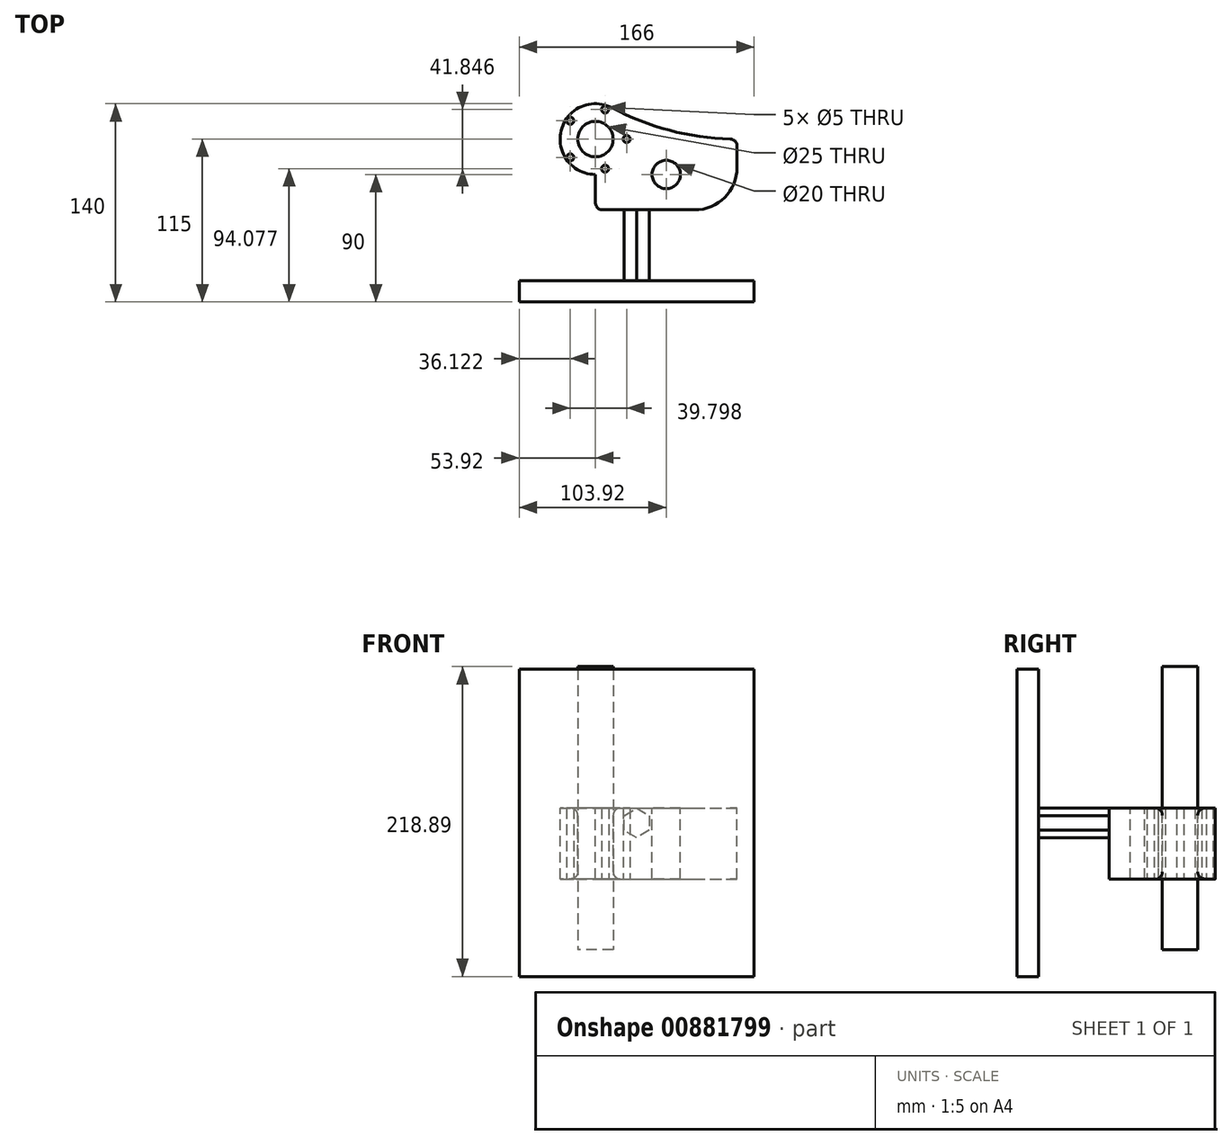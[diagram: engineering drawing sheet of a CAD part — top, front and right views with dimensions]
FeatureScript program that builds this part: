
annotation { "Feature Type Name" : "Feature", "Feature Type Description" : "" }
export const myFeature = defineFeature(function(context is Context, id is Id, definition is map)
    precondition{}
    {
        {
            var Q0;
            Q0=qCreatedBy(makeId("Top.planeOp"),FACE);
            var sketch = newSketch(context, id + "F0", { "sketchPlane" : qUnion([Q0])});
            skLineSegment(sketch, "E0.bottom", {"start": v(-50, -25) * mm, "end": v(50, -25) * mm});
            skLineSegment(sketch, "E0.top", {"start": v(-50, 25) * mm, "end": v(50, 25) * mm});
            skLineSegment(sketch, "E0.left", {"start": v(-50, -25) * mm, "end": v(-50, 25) * mm});
            skLineSegment(sketch, "E0.right", {"start": v(50, -25) * mm, "end": v(50, 25) * mm});
            skPoint(sketch, "E0.middle", {"position": v(0, 0) * mm});
            skCircle(sketch, "E1", {"center": v(-50, 25) * mm, "radius": 25 * mm});
            skArc(sketch, "E2", {"start": v(-38.24, 47.06) * mm, "mid": v(4.52, 30.6) * mm, "end": v(50, 25) * mm});
            skCircle(sketch, "E3", {"center": v(-50, 25) * mm, "radius": 12.5 * mm});
            skSolve(sketch);
        }
        {
            var Q0;
            {var subQ0=sQuery(id+"F0.wireOp",EDGE,"E2");Q0=makeQuery(id+"F0.imprint","IMPRINT",FACE,{"disambiguationData":[TD([[makeQuery(id+"F0.imprint","IMPRINT",EDGE,{"derivedFrom":subQ0}),-1.0]])]});}
            var Q1;
            {var subQ1=sQuery(id+"F0.wireOp",EDGE,"E0.bottom");Q1=makeQuery(id+"F0.imprint","IMPRINT",FACE,{"disambiguationData":[TD([[makeQuery(id+"F0.imprint","IMPRINT",EDGE,{"derivedFrom":subQ1}),1.0]])]});}
            var Q2;
            {var subQ4=sQuery(id+"F0.wireOp",EDGE,"E0.top");var subQ6=sQuery(id+"F0.wireOp",EDGE,"E3");var subQ8=makeQuery(id+"F0.imprint","INTERSECT",VERTEX,{"derivedFrom":[subQ4,subQ6]});Q2=makeQuery(id+"F0.imprint","IMPRINT",FACE,{"disambiguationData":[TD([[makeQuery(id+"F0.imprint","IMPRINT",EDGE,{"disambiguationData":[TD([[subQ8,-1.0]])],"derivedFrom":subQ4}),1.0]])]});}
            var Q3;
            {var subQ0=sQuery(id+"F0.wireOp",EDGE,"E3");var subQ1=sQuery(id+"F0.wireOp",EDGE,"E0.top");var subQ2=makeQuery(id+"F0.imprint","INTERSECT",VERTEX,{"derivedFrom":[subQ1,subQ0]});Q3=makeQuery(id+"F0.imprint","IMPRINT",FACE,{"disambiguationData":[TD([[makeQuery(id+"F0.imprint","IMPRINT",EDGE,{"disambiguationData":[TD([[subQ2,-1.0]])],"derivedFrom":subQ1}),-1.0]])]});}
            extrude(context, id + "F1", {"entities" : qUnion([Q0, Q1, Q2, Q3]), "oppositeDirection" : true, "depth" : 50 * mm, "offsetDistance" : 25 * mm});
        }
        {
            var Q0;
            {var subQ0=sQuery(id+"F0.wireOp",EDGE,"E0.left");var subQ1=sQuery(id+"F0.wireOp",EDGE,"E0.top");var subQ2=makeQuery(id+"F0.imprint","INTERSECT",VERTEX,{"derivedFrom":[subQ1,subQ0]});Q0=makeQuery(id+"F0.imprint","IMPRINT",FACE,{"disambiguationData":[TD([[makeQuery(id+"F0.imprint","IMPRINT",EDGE,{"disambiguationData":[TD([[subQ2,-1.0]])],"derivedFrom":subQ1}),1.0]])]});}
            var Q1;
            {var subQ0=sQuery(id+"F0.wireOp",EDGE,"E0.left");var subQ1=sQuery(id+"F0.wireOp",EDGE,"E0.top");var subQ2=makeQuery(id+"F0.imprint","INTERSECT",VERTEX,{"derivedFrom":[subQ1,subQ0]});Q1=makeQuery(id+"F0.imprint","IMPRINT",FACE,{"disambiguationData":[TD([[makeQuery(id+"F0.imprint","IMPRINT",EDGE,{"disambiguationData":[TD([[subQ2,-1.0]])],"derivedFrom":subQ1}),-1.0]])]});}
            extrude(context, id + "F2", {"entities" : qUnion([Q0, Q1]), "endBound" : BoundingType.SYMMETRIC, "depth" : 200 * mm, "offsetDistance" : 25 * mm});
        }
        {
            var Q0;
            Q0=makeQuery(id+"F1.opExtrude","SWEPT_FACE",FACE,{"disambiguationData":[OSD([sQuery(id+"F0.wireOp",EDGE,"E3")])]});
            fillet(context, id + "F3", {"entities" : qUnion([Q0]), "radius" : 5 * mm, "tangentPropagation" : true, "allowEdgeOverflow" : false});
        }
        {
            var Q0;
            Q0=makeQuery(id+"F1.opExtrude","SWEPT_EDGE",EDGE,{"disambiguationData":[OSD([sQuery(id+"F0.wireOp",EDGE,"E0.bottom"),sQuery(id+"F0.wireOp",EDGE,"E0.left")])]});
            var Q1;
            Q1=makeQuery(id+"F1.opExtrude","SWEPT_EDGE",EDGE,{"disambiguationData":[OSD([sQuery(id+"F0.wireOp",EDGE,"E0.top"),sQuery(id+"F0.wireOp",EDGE,"E0.right"),sQuery(id+"F0.wireOp",EDGE,"E2")])]});
            fillet(context, id + "F4", {"entities" : qUnion([Q0, Q1]), "radius" : 5 * mm, "tangentPropagation" : true, "allowEdgeOverflow" : false});
        }
        {
            var Q0;
            Q0=sQuery(id+"F0.wireOp",VERTEX,"E0.middle");
            var Q1;
            Q1=makeQuery(id+"F1.opExtrude","SWEPT_BODY",BODY,{"disambiguationData":[OSD([sQuery(id+"F0.wireOp",EDGE,"E0.bottom"),sQuery(id+"F0.wireOp",EDGE,"E0.left"),sQuery(id+"F0.wireOp",EDGE,"E0.right"),sQuery(id+"F0.wireOp",EDGE,"E1"),sQuery(id+"F0.wireOp",EDGE,"E2"),sQuery(id+"F0.wireOp",EDGE,"E3")])]});
            hole(context, id + "F5", {"style" : HoleStyle.SIMPLE, "endStyle" : HoleEndStyle.THROUGH, "holeDiameter" : 20 * mm, "majorDiameter" : 5 * mm, "isTappedThrough" : true, "tappedDepth" : 12 * mm, "tapClearance" : 3, "locations" : qUnion([Q0]), "scope" : qUnion([Q1])});
        }
        {
            var Q0;
            Q0=makeQuery(id+"F1.opExtrude","CAP_FACE",FACE,{"disambiguationData":[OSD([sQuery(id+"F0.wireOp",EDGE,"E0.bottom"),sQuery(id+"F0.wireOp",EDGE,"E0.left"),sQuery(id+"F0.wireOp",EDGE,"E0.right"),sQuery(id+"F0.wireOp",EDGE,"E1"),sQuery(id+"F0.wireOp",EDGE,"E2"),sQuery(id+"F0.wireOp",EDGE,"E3")])],"isStart":false});
            var sketch = newSketch(context, id + "F6", { "sketchPlane" : qUnion([Q0])});
            skLineSegment(sketch, "E4.0", {"start": v(-50, -25) * mm, "end": v(50, -25) * mm, "construction": true});
            skPoint(sketch, "E5", {"position": v(-28, -25) * mm});
            skPoint(sketch, "E6.0", {"position": v(-50, -25) * mm});
            skPoint(sketch, "E7.1.0", {"position": v(-43.2, -4.08) * mm});
            skPoint(sketch, "E7.2.0", {"position": v(-67.8, -12.07) * mm});
            skPoint(sketch, "E7.3.0", {"position": v(-67.8, -37.93) * mm});
            skPoint(sketch, "E7.4.0", {"position": v(-43.2, -45.92) * mm});
            skSolve(sketch);
        }
        {
            var Q0;
            Q0=sQuery(id+"F6.wireOp",VERTEX,"E7.4.0");
            var Q1;
            Q1=sQuery(id+"F6.wireOp",VERTEX,"E7.3.0");
            var Q2;
            Q2=sQuery(id+"F6.wireOp",VERTEX,"E7.2.0");
            var Q3;
            Q3=sQuery(id+"F6.wireOp",VERTEX,"E7.1.0");
            var Q4;
            Q4=sQuery(id+"F6.wireOp",VERTEX,"E5");
            var Q5;
            Q5=makeQuery(id+"F1.opExtrude","SWEPT_BODY",BODY,{"disambiguationData":[OSD([sQuery(id+"F0.wireOp",EDGE,"E0.bottom"),sQuery(id+"F0.wireOp",EDGE,"E0.left"),sQuery(id+"F0.wireOp",EDGE,"E0.right"),sQuery(id+"F0.wireOp",EDGE,"E1"),sQuery(id+"F0.wireOp",EDGE,"E2"),sQuery(id+"F0.wireOp",EDGE,"E3")])]});
            hole(context, id + "F7", {"style" : HoleStyle.SIMPLE, "endStyle" : HoleEndStyle.THROUGH, "standardTappedOrClearance" : lookupTablePath({ "standard" : "ISO", "size" : "5", "type" : "Drilled" }), "standardBlindInLast" : lookupTablePath({ "standard" : "ISO", "size" : "5", "type" : "Drilled" }), "holeDiameter" : 5 * mm, "majorDiameter" : 5 * mm, "isTappedThrough" : true, "tappedDepth" : 12 * mm, "tapClearance" : 3, "locations" : qUnion([Q0, Q1, Q2, Q3, Q4]), "scope" : qUnion([Q5])});
        }
        {
            var Q0;
            Q0=makeQuery(id+"F1.opExtrude","SWEPT_EDGE",EDGE,{"disambiguationData":[OSD([sQuery(id+"F0.wireOp",EDGE,"E0.bottom"),sQuery(id+"F0.wireOp",EDGE,"E0.right")])]});
            fillet(context, id + "F8", {"entities" : qUnion([Q0]), "radius" : 30 * mm, "tangentPropagation" : true, "allowEdgeOverflow" : false});
        }
        {
            var Q0;
            Q0=makeQuery(id+"F1.opExtrude","SWEPT_FACE",FACE,{"disambiguationData":[OSD([sQuery(id+"F0.wireOp",EDGE,"E0.bottom")])]});
            var sketch = newSketch(context, id + "F9", { "sketchPlane" : qUnion([Q0])});
            skCircle(sketch, "E8.cCircle", {"center": v(-20.92, -10.4) * mm, "radius": 9 * mm, "construction": true});
            skLineSegment(sketch, "E8.0", {"start": v(-11.92, -5.2) * mm, "end": v(-11.92, -15.59) * mm});
            skLineSegment(sketch, "E8.1", {"start": v(-11.92, -15.59) * mm, "end": v(-20.92, -20.78) * mm});
            skLineSegment(sketch, "E8.2", {"start": v(-20.92, -20.78) * mm, "end": v(-29.92, -15.59) * mm});
            skLineSegment(sketch, "E8.3", {"start": v(-29.92, -15.59) * mm, "end": v(-29.92, -5.2) * mm});
            skLineSegment(sketch, "E8.4", {"start": v(-29.92, -5.2) * mm, "end": v(-20.92, 0) * mm});
            skLineSegment(sketch, "E8.5", {"start": v(-20.92, 0) * mm, "end": v(-11.92, -5.2) * mm});
            skPoint(sketch, "E8.0.midPoint", {"position": v(-11.92, -10.4) * mm});
            skSolve(sketch);
        }
        {
            var Q0;
            Q0=makeQuery(id+"F9.imprint","IMPRINT",FACE,{"disambiguationData":[TD([[makeQuery(id+"F9.imprint","IMPRINT",EDGE,{"derivedFrom":sQuery(id+"F9.wireOp",EDGE,"E8.0")}),-1.0]])]});
            extrude(context, id + "F10", {"entities" : qUnion([Q0]), "depth" : 50 * mm, "offsetDistance" : 25 * mm});
        }
        {
            var Q0;
            Q0=makeQuery(id+"F10.opExtrude","CAP_FACE",FACE,{"disambiguationData":[OSD([sQuery(id+"F9.wireOp",EDGE,"E8.0"),sQuery(id+"F9.wireOp",EDGE,"E8.1"),sQuery(id+"F9.wireOp",EDGE,"E8.2"),sQuery(id+"F9.wireOp",EDGE,"E8.3"),sQuery(id+"F9.wireOp",EDGE,"E8.4"),sQuery(id+"F9.wireOp",EDGE,"E8.5")])],"isStart":false});
            var sketch = newSketch(context, id + "F11", { "sketchPlane" : qUnion([Q0])});
            skPoint(sketch, "E9.0", {"position": v(-20.92, -10.4) * mm});
            skLineSegment(sketch, "E10.bottom", {"start": v(-103.92, -118.9) * mm, "end": v(62.08, -118.9) * mm});
            skLineSegment(sketch, "E10.top", {"start": v(-103.92, 98.1) * mm, "end": v(62.08, 98.1) * mm});
            skLineSegment(sketch, "E10.left", {"start": v(-103.92, -118.9) * mm, "end": v(-103.92, 98.1) * mm});
            skLineSegment(sketch, "E10.right", {"start": v(62.08, -118.9) * mm, "end": v(62.08, 98.1) * mm});
            skSolve(sketch);
        }
        {
            var Q0;
            Q0=makeQuery(id+"F11.imprint","IMPRINT",FACE,{"disambiguationData":[TD([[makeQuery(id+"F11.imprint","IMPRINT",EDGE,{"derivedFrom":sQuery(id+"F11.wireOp",EDGE,"E10.bottom")}),1.0]])]});
            var Q1;
            Q1=makeQuery(id+"F11.imprint","IMPRINT",FACE,{"disambiguationData":[TD([[makeQuery(id+"F11.imprint","IMPRINT",EDGE,{"derivedFrom":makeQuery(id+"F10.opExtrude","CAP_EDGE",EDGE,{"disambiguationData":[OSD([sQuery(id+"F9.wireOp",EDGE,"E8.0")])],"isStart":false})}),-1.0]])]});
            extrude(context, id + "F12", {"entities" : qUnion([Q0, Q1]), "depth" : 15 * mm, "offsetDistance" : 25 * mm});
        }
    });
